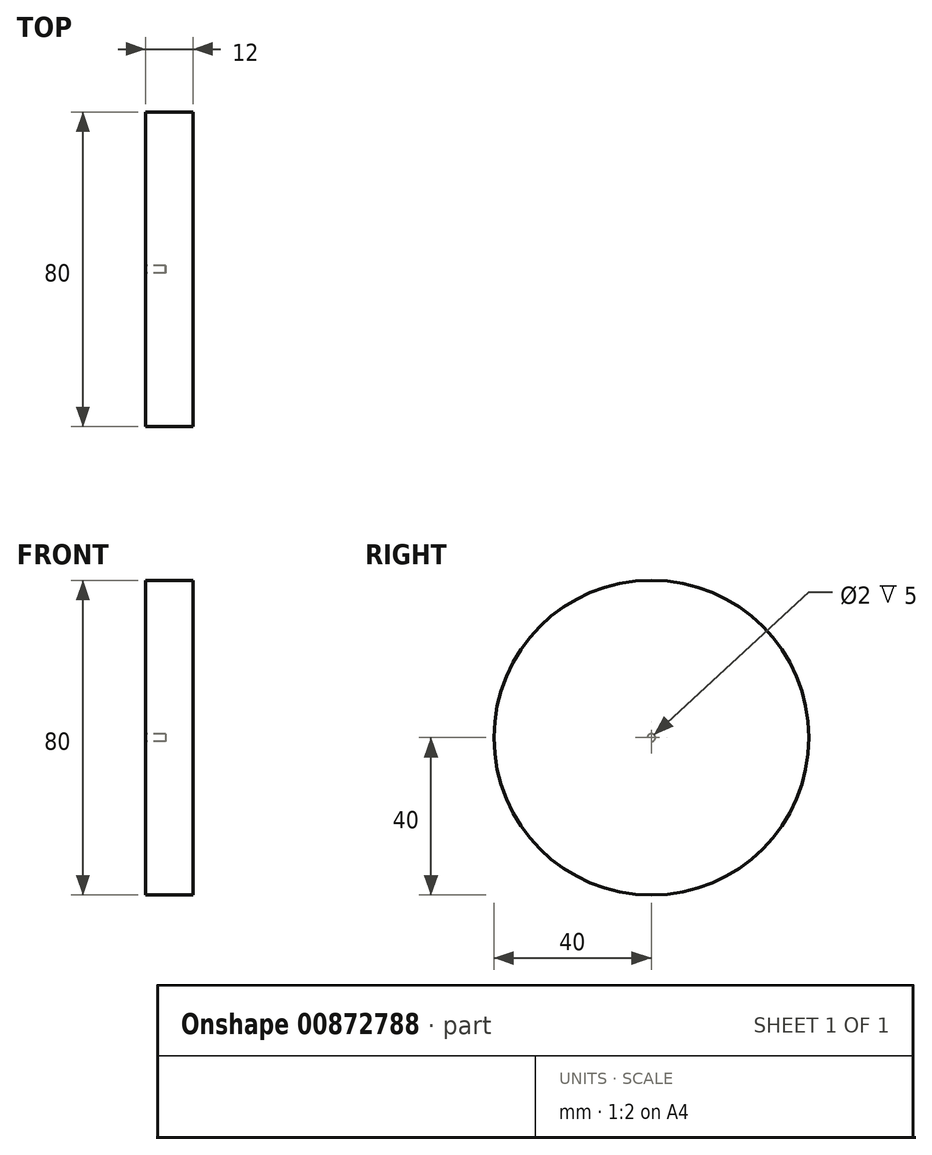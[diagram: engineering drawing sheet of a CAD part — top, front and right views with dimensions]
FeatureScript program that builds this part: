
annotation { "Feature Type Name" : "Feature", "Feature Type Description" : "" }
export const myFeature = defineFeature(function(context is Context, id is Id, definition is map)
    precondition{}
    {
        {
            var Q0;
            Q0=qCreatedBy(makeId("Right.planeOp"),FACE);
            var sketch = newSketch(context, id + "F0", { "sketchPlane" : qUnion([Q0])});
            skCircle(sketch, "E0", {"center": v(0, 0) * mm, "radius": 40 * mm});
            skSolve(sketch);
        }
        {
            var Q0;
            Q0=makeQuery(id+"F0.imprint","IMPRINT",FACE,{"disambiguationData":[TD([[makeQuery(id+"F0.imprint","IMPRINT",EDGE,{"derivedFrom":sQuery(id+"F0.wireOp",EDGE,"E0")}),1.0]])]});
            extrude(context, id + "F1", {"entities" : qUnion([Q0]), "depth" : 12 * mm, "offsetDistance" : 25 * mm});
        }
        {
            var Q0;
            Q0=makeQuery(id+"F1.opExtrude","CAP_FACE",FACE,{"disambiguationData":[OSD([sQuery(id+"F0.wireOp",EDGE,"E0")])],"isStart":true});
            var sketch = newSketch(context, id + "F2", { "sketchPlane" : qUnion([Q0])});
            skCircle(sketch, "E1", {"center": v(0, 0) * mm, "radius": 1 * mm});
            skSolve(sketch);
        }
        {
            var Q0;
            Q0 = qSketchRegion(id + "F2", true);
            extrude(context, id + "F3", {"entities" : qUnion([Q0]), "operationType" : NewBodyOperationType.REMOVE, "oppositeDirection" : true, "depth" : 5 * mm, "offsetDistance" : 25 * mm});
        }
    });
